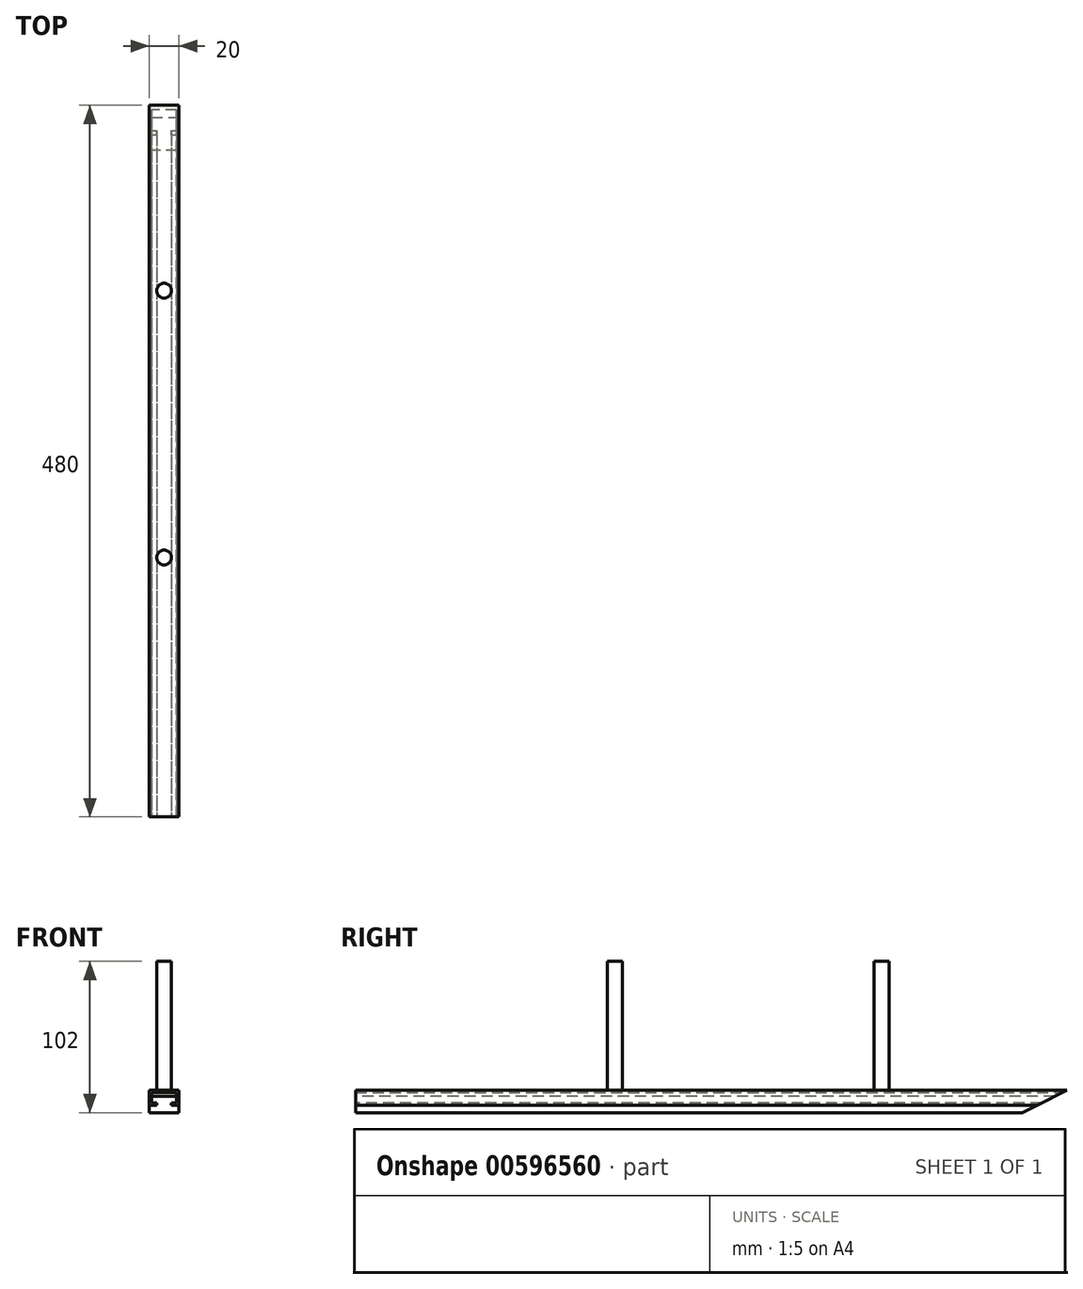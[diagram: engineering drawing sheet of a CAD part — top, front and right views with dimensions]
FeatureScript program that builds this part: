
annotation { "Feature Type Name" : "Feature", "Feature Type Description" : "" }
export const myFeature = defineFeature(function(context is Context, id is Id, definition is map)
    precondition{}
    {
        {
            var Q0;
            Q0=qCreatedBy(makeId("Front.planeOp"),FACE);
            var sketch = newSketch(context, id + "F0", { "sketchPlane" : qUnion([Q0])});
            skLineSegment(sketch, "E0.bottom", {"start": v(-10, -5) * mm, "end": v(-5, -5) * mm});
            skLineSegment(sketch, "E0.top", {"start": v(-10, 5) * mm, "end": v(10, 5) * mm});
            skLineSegment(sketch, "E0.left", {"start": v(-10, -5) * mm, "end": v(-10, 5) * mm});
            skLineSegment(sketch, "E0.right", {"start": v(10, -5) * mm, "end": v(10, 5) * mm});
            skLineSegment(sketch, "E1.0", {"start": v(-8.5, 3.5) * mm, "end": v(8.5, 3.5) * mm});
            skLineSegment(sketch, "E2.0", {"start": v(-8.5, -3.5) * mm, "end": v(-8.5, 3.5) * mm});
            skLineSegment(sketch, "E3.0", {"start": v(-8.5, -3.5) * mm, "end": v(-5, -3.5) * mm});
            skLineSegment(sketch, "E4.0", {"start": v(8.5, -3.5) * mm, "end": v(8.5, 3.5) * mm});
            skLineSegment(sketch, "E5.0", {"start": v(-5, -5) * mm, "end": v(-5, -3.5) * mm});
            skLineSegment(sketch, "E6.0", {"start": v(5, -5) * mm, "end": v(5, -3.5) * mm});
            skLineSegment(sketch, "E7.trimOffspring", {"start": v(5, -3.5) * mm, "end": v(8.5, -3.5) * mm});
            skLineSegment(sketch, "E8.trimOffspring", {"start": v(5, -5) * mm, "end": v(10, -5) * mm});
            skSolve(sketch);
        }
        {
            var Q0;
            Q0 = qSketchRegion(id + "F0", true);
            extrude(context, id + "F1", {"entities" : qUnion([Q0]), "depth" : 480 * mm, "offsetDistance" : 25 * mm});
        }
        {
            var Q0;
            Q0=makeQuery(id+"F1.opExtrude","CAP_FACE",FACE,{"disambiguationData":[OSD([sQuery(id+"F0.wireOp",EDGE,"E0.bottom"),sQuery(id+"F0.wireOp",EDGE,"E0.top"),sQuery(id+"F0.wireOp",EDGE,"E0.left"),sQuery(id+"F0.wireOp",EDGE,"E0.right"),sQuery(id+"F0.wireOp",EDGE,"E1.0"),sQuery(id+"F0.wireOp",EDGE,"E2.0"),sQuery(id+"F0.wireOp",EDGE,"E3.0"),sQuery(id+"F0.wireOp",EDGE,"E4.0"),sQuery(id+"F0.wireOp",EDGE,"E5.0"),sQuery(id+"F0.wireOp",EDGE,"E6.0"),sQuery(id+"F0.wireOp",EDGE,"E7.trimOffspring"),sQuery(id+"F0.wireOp",EDGE,"E8.trimOffspring")])],"isStart":false});
            var sketch = newSketch(context, id + "F2", { "sketchPlane" : qUnion([Q0])});
            skLineSegment(sketch, "E9.0", {"start": v(-8.5, 1) * mm, "end": v(0, 1) * mm});
            skLineSegment(sketch, "E10.0", {"start": v(-8.5, -10) * mm, "end": v(0, -10) * mm});
            skLineSegment(sketch, "E11", {"start": v(-8.5, 1) * mm, "end": v(-8.5, -3.5) * mm});
            skLineSegment(sketch, "E12", {"start": v(-8.5, -3.5) * mm, "end": v(-5, -3.5) * mm});
            skLineSegment(sketch, "E13", {"start": v(-5, -3.5) * mm, "end": v(-5, -5) * mm});
            skLineSegment(sketch, "E14", {"start": v(-5, -5) * mm, "end": v(-10, -5) * mm});
            skLineSegment(sketch, "E15", {"start": v(-10, -5) * mm, "end": v(-10, -10) * mm});
            skLineSegment(sketch, "E16", {"start": v(-10, -10) * mm, "end": v(-8.5, -10) * mm});
            skLineSegment(sketch, "E17.MirrorCS", {"start": v(8.5, 1) * mm, "end": v(0, 1) * mm});
            skLineSegment(sketch, "E18.MirrorCS", {"start": v(8.5, 1) * mm, "end": v(8.5, -3.5) * mm});
            skLineSegment(sketch, "E19.MirrorCS", {"start": v(8.5, -3.5) * mm, "end": v(5, -3.5) * mm});
            skLineSegment(sketch, "E20.MirrorCS", {"start": v(5, -3.5) * mm, "end": v(5, -5) * mm});
            skLineSegment(sketch, "E21.MirrorCS", {"start": v(5, -5) * mm, "end": v(10, -5) * mm});
            skLineSegment(sketch, "E22.MirrorCS", {"start": v(10, -5) * mm, "end": v(10, -10) * mm});
            skLineSegment(sketch, "E23.MirrorCS", {"start": v(10, -10) * mm, "end": v(8.5, -10) * mm});
            skLineSegment(sketch, "E24.MirrorCS", {"start": v(8.5, -10) * mm, "end": v(0, -10) * mm});
            skSolve(sketch);
        }
        {
            var Q0;
            Q0=makeQuery(id+"F2.imprint","IMPRINT",FACE,{"disambiguationData":[TD([[makeQuery(id+"F2.imprint","IMPRINT",EDGE,{"derivedFrom":sQuery(id+"F2.wireOp",EDGE,"E9.0")}),-1.0]])]});
            extrude(context, id + "F3", {"entities" : qUnion([Q0]), "oppositeDirection" : true, "depth" : 480 * mm, "offsetDistance" : 25 * mm});
        }
        {
            var Q0;
            Q0=makeQuery(id+"F1.opExtrude","SWEPT_FACE",FACE,{"disambiguationData":[OSD([sQuery(id+"F0.wireOp",EDGE,"E0.right")])]});
            var sketch = newSketch(context, id + "F4", { "sketchPlane" : qUnion([Q0])});
            skLineSegment(sketch, "E25", {"start": v(0, 5) * mm, "end": v(0, -10) * mm});
            skLineSegment(sketch, "E26", {"start": v(0, -10) * mm, "end": v(-30, -10) * mm});
            skLineSegment(sketch, "E27", {"start": v(-30, -10) * mm, "end": v(0, 5) * mm});
            skSolve(sketch);
        }
        {
            var Q0;
            Q0 = qSketchRegion(id + "F4", true);
            extrude(context, id + "F5", {"entities" : qUnion([Q0]), "operationType" : NewBodyOperationType.REMOVE, "oppositeDirection" : true, "depth" : 25 * mm, "offsetDistance" : 25 * mm});
        }
        {
            var Q0;
            Q0=makeQuery(id+"F1.opExtrude","SWEPT_FACE",FACE,{"disambiguationData":[OSD([sQuery(id+"F0.wireOp",EDGE,"E0.top")])]});
            var sketch = newSketch(context, id + "F6", { "sketchPlane" : qUnion([Q0])});
            skCircle(sketch, "E28", {"center": v(0, -305) * mm, "radius": 5 * mm});
            skPoint(sketch, "E28.centerSnap0", {"position": v(0, -480) * mm});
            skCircle(sketch, "E29", {"center": v(0, -125) * mm, "radius": 5 * mm});
            skSolve(sketch);
        }
        {
            var Q0;
            Q0 = qSketchRegion(id + "F6", true);
            extrude(context, id + "F7", {"entities" : qUnion([Q0]), "operationType" : NewBodyOperationType.ADD, "depth" : 87 * mm, "offsetDistance" : 25 * mm});
        }
    });
